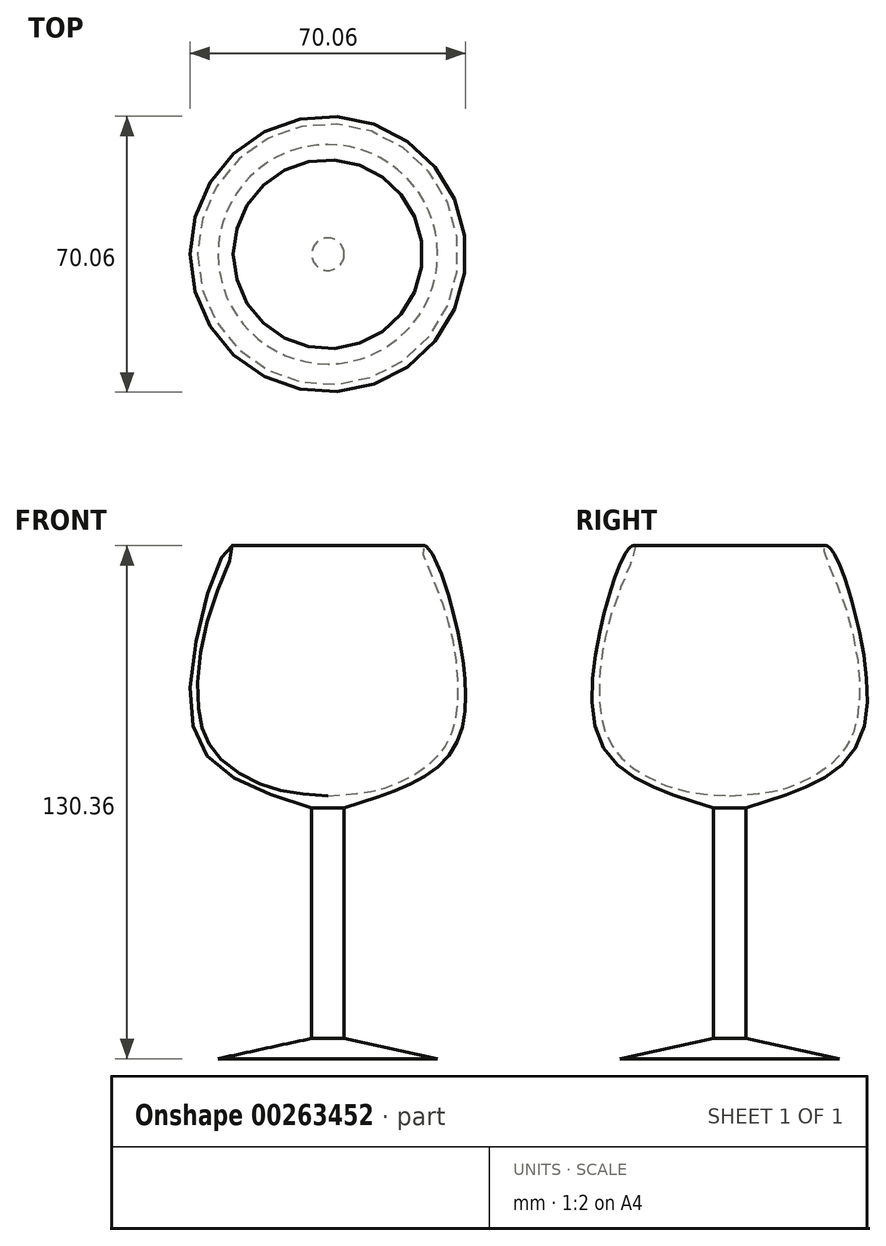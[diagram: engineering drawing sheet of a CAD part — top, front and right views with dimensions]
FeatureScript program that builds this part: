
annotation { "Feature Type Name" : "Feature", "Feature Type Description" : "" }
export const myFeature = defineFeature(function(context is Context, id is Id, definition is map)
    precondition{}
    {
        {
            var Q0;
            Q0=qCreatedBy(makeId("Front.planeOp"),FACE);
            var sketch = newSketch(context, id + "F0", { "sketchPlane" : qUnion([Q0])});
            skLineSegment(sketch, "E0", {"start": v(0, -76.08) * mm, "end": v(-27.89, -76.08) * mm});
            skLineSegment(sketch, "E1", {"start": v(-27.89, -76.08) * mm, "end": v(-4.13, -70.92) * mm});
            skLineSegment(sketch, "E2", {"start": v(-4.13, -70.92) * mm, "end": v(-4.13, -12.4) * mm});
            skFitSpline(sketch, "E3", {"points": [v(-4.13, -12.4) * mm, v(-29.95, 0) * mm, v(-34.43, 24.1) * mm, v(-25.48, 53.7) * mm, v(-24.1, 54.05) * mm, v(-27.89, 43.03) * mm, v(-32.7, 24.79) * mm, v(-32.7, 11.36) * mm, v(-30.98, 5.5) * mm, v(-27.2, 0) * mm, v(-18.94, -5.5) * mm, v(-10.67, -8.26) * mm, v(0, -9.3) * mm], "startDerivative": vector(-245.59, 76.44) * mm, "endDerivative": vector(145.72, -8.3) * mm});
            skLineSegment(sketch, "E4", {"start": v(0, -76.08) * mm, "end": v(0, -9.3) * mm});
            skSolve(sketch);
        }
        {
            var Q0;
            Q0=makeQuery(id+"F0.imprint","IMPRINT",FACE,{"disambiguationData":[TD([[makeQuery(id+"F0.imprint","IMPRINT",EDGE,{"derivedFrom":sQuery(id+"F0.wireOp",EDGE,"E0")}),-1.0]])]});
            var Q1;
            Q1=sQuery(id+"F0.wireOp",EDGE,"E4");
            revolve(context, id + "F1", {"entities" : qUnion([Q0]), "axis" : qUnion([Q1]), "revolveType" : RevolveType.FULL});
        }
    });
